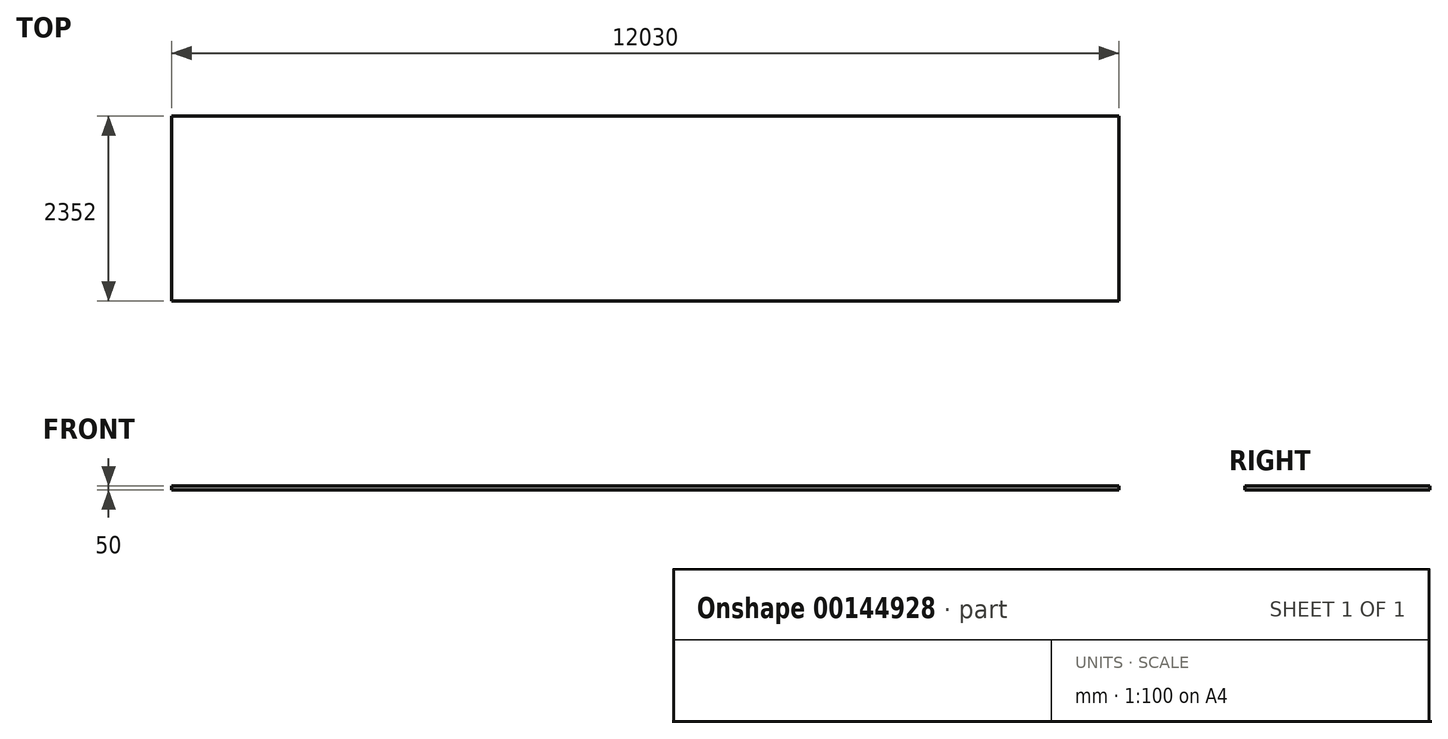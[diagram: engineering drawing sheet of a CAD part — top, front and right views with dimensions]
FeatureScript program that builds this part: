
annotation { "Feature Type Name" : "Feature", "Feature Type Description" : "" }
export const myFeature = defineFeature(function(context is Context, id is Id, definition is map)
    precondition{}
    {
        {
            var Q0;
            Q0=qCreatedBy(makeId("Top.planeOp"),FACE);
            var sketch = newSketch(context, id + "F0", { "sketchPlane" : qUnion([Q0])});
            skLineSegment(sketch, "E0.bottom", {"start": v(6015, -1176) * mm, "end": v(-6015, -1176) * mm});
            skLineSegment(sketch, "E0.top", {"start": v(6015, 1176) * mm, "end": v(-6015, 1176) * mm});
            skLineSegment(sketch, "E0.left", {"start": v(6015, -1176) * mm, "end": v(6015, 1176) * mm});
            skLineSegment(sketch, "E0.right", {"start": v(-6015, -1176) * mm, "end": v(-6015, 1176) * mm});
            skPoint(sketch, "E0.middle", {"position": v(0, 0) * mm});
            skSolve(sketch);
        }
        {
            var Q0;
            Q0=makeQuery(id+"F0.imprint","IMPRINT",FACE,{"disambiguationData":[TD([[makeQuery(id+"F0.imprint","IMPRINT",EDGE,{"derivedFrom":sQuery(id+"F0.wireOp",EDGE,"E0.bottom")}),-1.0]])]});
            extrude(context, id + "F2", {"entities" : qUnion([Q0]), "depth" : 50 * mm});
        }
    });
